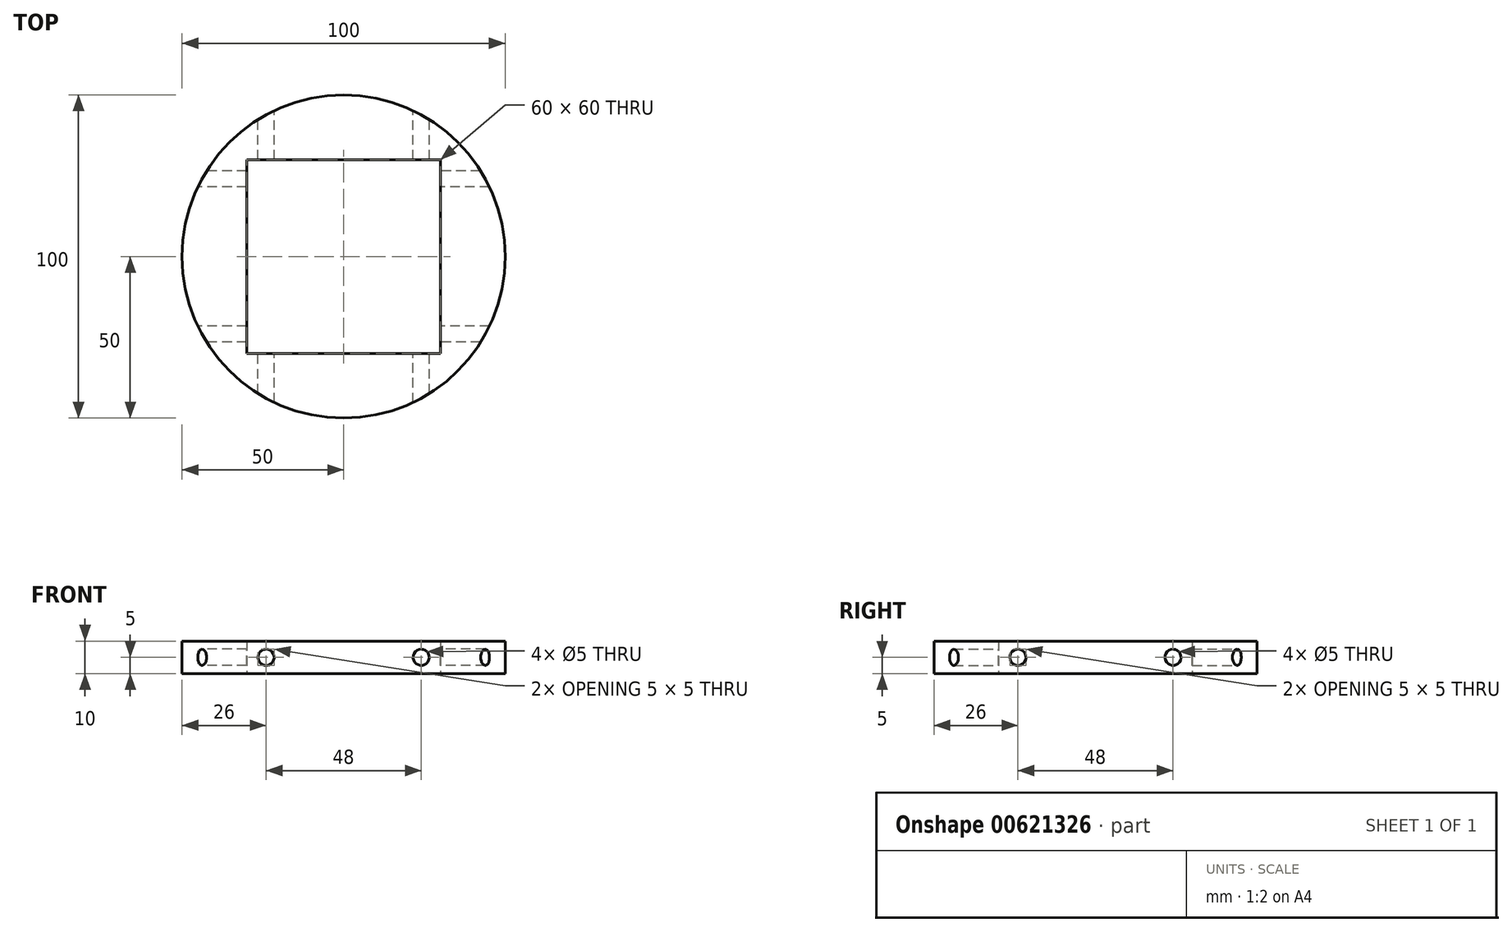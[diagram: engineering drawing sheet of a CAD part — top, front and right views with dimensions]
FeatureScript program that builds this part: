
annotation { "Feature Type Name" : "Feature", "Feature Type Description" : "" }
export const myFeature = defineFeature(function(context is Context, id is Id, definition is map)
    precondition{}
    {
        {
            assignVariable(context, id + "F0", {"name" : "part_height", "anyValue" : 10});
        }
        {
            var Q0;
            Q0=qCreatedBy(makeId("Top.planeOp"),FACE);
            var sketch = newSketch(context, id + "F1", { "sketchPlane" : qUnion([Q0])});
            skLineSegment(sketch, "E0.bottom", {"start": v(30, 30) * mm, "end": v(-30, 30) * mm});
            skLineSegment(sketch, "E0.top", {"start": v(30, -30) * mm, "end": v(-30, -30) * mm});
            skLineSegment(sketch, "E0.left", {"start": v(30, 30) * mm, "end": v(30, -30) * mm});
            skLineSegment(sketch, "E0.right", {"start": v(-30, 30) * mm, "end": v(-30, -30) * mm});
            skPoint(sketch, "E0.middle", {"position": v(0, 0) * mm});
            skCircle(sketch, "E1", {"center": v(0, 0) * mm, "radius": 50 * mm});
            skSolve(sketch);
        }
        {
            var Q0;
            Q0 = qSketchRegion(id + "F1", true);
            extrude(context, id + "F2", {"entities" : qUnion([Q0]), "depth" : (getVariable(context, 'part_height')) * mm, "offsetDistance" : 25 * mm});
        }
        {
            var Q0;
            Q0=makeQuery(id+"F2.opExtrude","SWEPT_FACE",FACE,{"disambiguationData":[OSD([sQuery(id+"F1.wireOp",EDGE,"E0.bottom")])]});
            var sketch = newSketch(context, id + "F3", { "sketchPlane" : qUnion([Q0])});
            skLineSegment(sketch, "E2", {"start": v(0, 2.61) * mm, "end": v(0, 26.9) * mm});
            skPoint(sketch, "E2.endSnap0", {"position": v(0, 10) * mm});
            skCircle(sketch, "E3", {"center": v(-24, 5) * mm, "radius": 2.5 * mm});
            skPoint(sketch, "E3.centerSnap0", {"position": v(-30, 5) * mm});
            skCircle(sketch, "E4.MirrorC", {"center": v(24, 5) * mm, "radius": 2.5 * mm});
            skSolve(sketch);
        }
        {
            var Q0;
            Q0 = qSketchRegion(id + "F3", true);
            extrude(context, id + "F4", {"entities" : qUnion([Q0]), "endBound" : BoundingType.SYMMETRIC, "depth" : 290 * mm, "offsetDistance" : 25 * mm});
        }
        {
            var Q0;
            Q0=qCreatedBy(makeId("Right.planeOp"),FACE);
            var sketch = newSketch(context, id + "F5", { "sketchPlane" : qUnion([Q0])});
            skLineSegment(sketch, "E5", {"start": v(0, 0) * mm, "end": v(0, 45.66) * mm, "construction": true});
            skSolve(sketch);
        }
        {
            var Q0;
            Q0=makeQuery(id+"F4.opExtrude","SWEPT_BODY",BODY,{"disambiguationData":[OSD([sQuery(id+"F3.wireOp",EDGE,"E3")])]});
            var Q1;
            Q1=makeQuery(id+"F4.opExtrude","SWEPT_BODY",BODY,{"disambiguationData":[OSD([sQuery(id+"F3.wireOp",EDGE,"E4.MirrorC")])]});
            var Q2;
            Q2=sQuery(id+"F5.wireOp",EDGE,"E5");
            circularPattern(context, id + "F6", {"entities" : qUnion([Q0, Q1]), "axis" : qUnion([Q2]), "angle" : 90 * degree, "instanceCount" : 2, "equalSpace" : true});
        }
        {
            var Q0;
            Q0=makeQuery(id+"F4.opExtrude","SWEPT_BODY",BODY,{"disambiguationData":[OSD([sQuery(id+"F3.wireOp",EDGE,"E3")])]});
            var Q1;
            Q1=makeQuery(id+"F6.opPattern","COPY",BODY,{"derivedFrom":makeQuery(id+"F4.opExtrude","SWEPT_BODY",BODY,{"disambiguationData":[OSD([sQuery(id+"F3.wireOp",EDGE,"E4.MirrorC")])]}),"instanceName":"1"});
            var Q2;
            Q2=makeQuery(id+"F4.opExtrude","SWEPT_BODY",BODY,{"disambiguationData":[OSD([sQuery(id+"F3.wireOp",EDGE,"E4.MirrorC")])]});
            var Q3;
            Q3=makeQuery(id+"F6.opPattern","COPY",BODY,{"derivedFrom":makeQuery(id+"F4.opExtrude","SWEPT_BODY",BODY,{"disambiguationData":[OSD([sQuery(id+"F3.wireOp",EDGE,"E3")])]}),"instanceName":"1"});
            var Q4;
            Q4=makeQuery(id+"F2.opExtrude","SWEPT_BODY",BODY,{"disambiguationData":[OSD([sQuery(id+"F1.wireOp",EDGE,"E0.bottom"),sQuery(id+"F1.wireOp",EDGE,"E0.top"),sQuery(id+"F1.wireOp",EDGE,"E0.left"),sQuery(id+"F1.wireOp",EDGE,"E0.right"),sQuery(id+"F1.wireOp",EDGE,"E1")])]});
            booleanBodies(context, id + "F7", {"operationType" : BooleanOperationType.SUBTRACTION, "tools" : qUnion([Q0, Q1, Q2, Q3]), "targets" : qUnion([Q4])});
        }
    });
